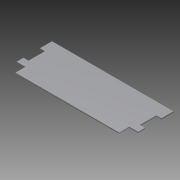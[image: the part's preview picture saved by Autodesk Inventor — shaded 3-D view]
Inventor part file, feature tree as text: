
AUTODESK INVENTOR PART (.ipt)
format: ipt  version: 2012 (Build 160160000, 160)  size: 100,352 bytes
history: native  units: in
note: dims shown in document units (in); Inventor stores cm internally (conversion verified against a paired STEP export)
features: extrude x2, sketch x2
ambient origin geometry x8: Origin, YZ Plane, XZ Plane, XY Plane, X Axis, Y Axis, Z Axis, Center Point
bodies: Solid1 (feature_tree)
feature tree (4):
  extrude  "Extrusion1"  Depth=0.2in
  extrude  "Extrusion2"  Depth=1.75in
  sketch  "Sketch1"  dims[d0=24.0in d1=0.2in]
  sketch  "Sketch2"  dims[d2=9.0in d3=0.0in d4=1.75in d5=2.0in d6=1.75in d7=2.0in d8=2.4in d9=2.4in d10=1.0in d11=1.0in d12=3.25in d13=3.25in d14=1.0in d15=0.0in]
